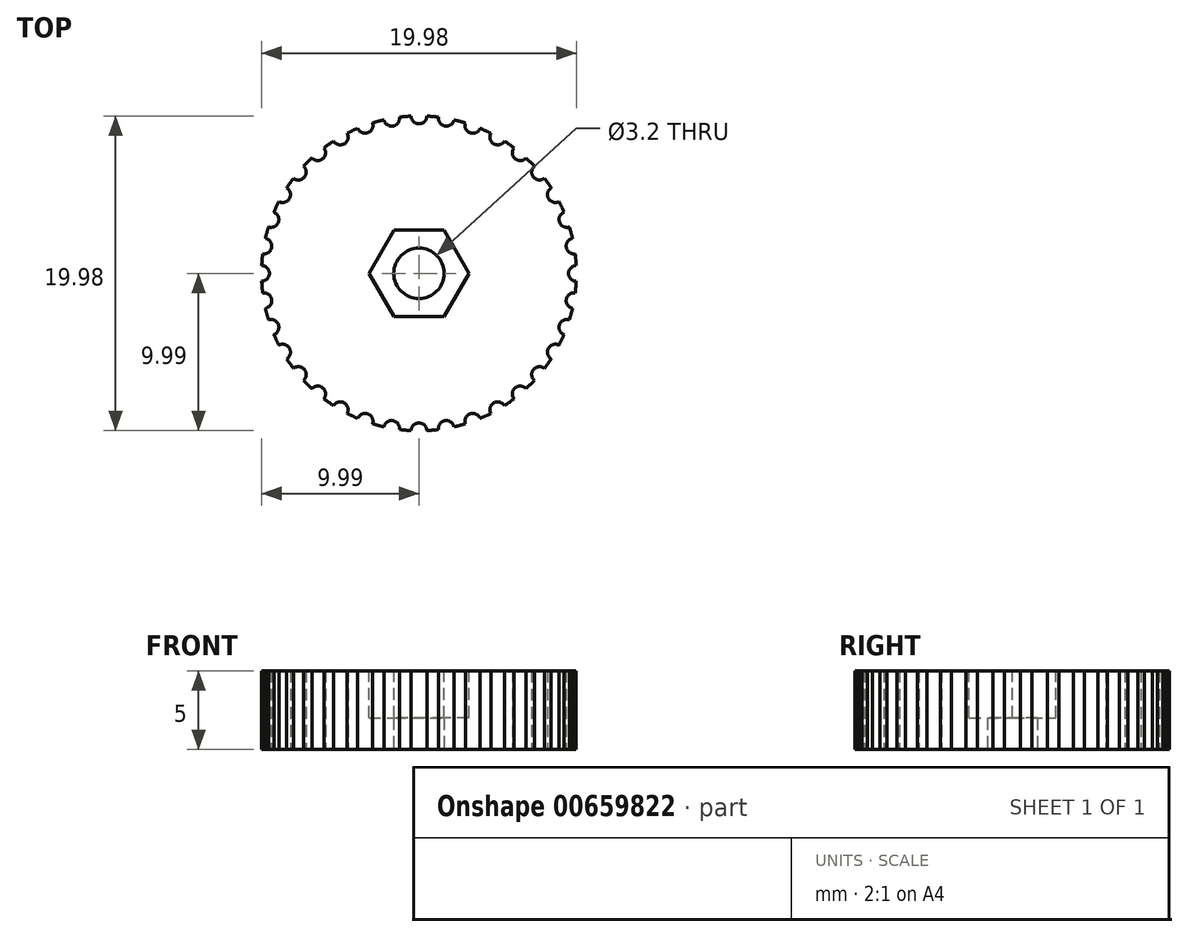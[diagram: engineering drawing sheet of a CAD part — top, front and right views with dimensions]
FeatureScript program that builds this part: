
annotation { "Feature Type Name" : "Feature", "Feature Type Description" : "" }
export const myFeature = defineFeature(function(context is Context, id is Id, definition is map)
    precondition{}
    {
        {
            var Q0;
            Q0=qCreatedBy(makeId("Top.planeOp"),FACE);
            var sketch = newSketch(context, id + "F0", { "sketchPlane" : qUnion([Q0])});
            skCircle(sketch, "E0", {"center": v(0, 0) * mm, "radius": 1.6 * mm});
            skArc(sketch, "E1", {"start": v(-0.5, 9.99) * mm, "mid": v(0, 9.5) * mm, "end": v(0.5, 9.99) * mm});
            skLineSegment(sketch, "E2.anchor1", {"start": v(0, 0) * mm, "end": v(0, 10) * mm, "construction": true});
            skArc(sketch, "E3", {"start": v(0.87, 9.96) * mm, "mid": v(0.69, 9.98) * mm, "end": v(0.5, 9.99) * mm});
            skLineSegment(sketch, "E4", {"start": v(0, 0) * mm, "end": v(0.87, 9.96) * mm, "construction": true});
            skLineSegment(sketch, "E5", {"start": v(0, 0) * mm, "end": v(-0.87, 9.96) * mm, "construction": true});
            skArc(sketch, "E6.trimOffspring", {"start": v(-0.5, 9.99) * mm, "mid": v(-0.69, 9.98) * mm, "end": v(-0.87, 9.96) * mm});
            skArc(sketch, "E7.1.0", {"start": v(-2.23, 9.75) * mm, "mid": v(-2.4, 9.7) * mm, "end": v(-2.59, 9.66) * mm});
            skArc(sketch, "E7.1.1", {"start": v(-2.23, 9.75) * mm, "mid": v(-1.65, 9.36) * mm, "end": v(-1.24, 9.92) * mm});
            skArc(sketch, "E7.1.2", {"start": v(-0.87, 9.96) * mm, "mid": v(-1.06, 9.94) * mm, "end": v(-1.24, 9.92) * mm});
            skArc(sketch, "E7.2.0", {"start": v(-3.89, 9.21) * mm, "mid": v(-4.06, 9.14) * mm, "end": v(-4.23, 9.06) * mm});
            skArc(sketch, "E7.2.1", {"start": v(-3.89, 9.21) * mm, "mid": v(-3.25, 8.93) * mm, "end": v(-2.95, 9.56) * mm});
            skArc(sketch, "E7.2.2", {"start": v(-2.59, 9.66) * mm, "mid": v(-2.77, 9.6) * mm, "end": v(-2.95, 9.56) * mm});
            skArc(sketch, "E7.3.0", {"start": v(-5.43, 8.4) * mm, "mid": v(-5.58, 8.3) * mm, "end": v(-5.74, 8.2) * mm});
            skArc(sketch, "E7.3.1", {"start": v(-5.43, 8.4) * mm, "mid": v(-4.75, 8.23) * mm, "end": v(-4.56, 8.9) * mm});
            skArc(sketch, "E7.3.2", {"start": v(-4.23, 9.06) * mm, "mid": v(-4.4, 8.98) * mm, "end": v(-4.56, 8.9) * mm});
            skArc(sketch, "E7.4.0", {"start": v(-6.8, 7.33) * mm, "mid": v(-6.94, 7.2) * mm, "end": v(-7.07, 7.07) * mm});
            skArc(sketch, "E7.4.1", {"start": v(-6.8, 7.33) * mm, "mid": v(-6.1, 7.28) * mm, "end": v(-6.04, 7.97) * mm});
            skArc(sketch, "E7.4.2", {"start": v(-5.74, 8.2) * mm, "mid": v(-5.89, 8.08) * mm, "end": v(-6.04, 7.97) * mm});
            skArc(sketch, "E7.5.0", {"start": v(-7.97, 6.04) * mm, "mid": v(-8.08, 5.89) * mm, "end": v(-8.2, 5.74) * mm});
            skArc(sketch, "E7.5.1", {"start": v(-7.97, 6.04) * mm, "mid": v(-7.28, 6.1) * mm, "end": v(-7.33, 6.8) * mm});
            skArc(sketch, "E7.5.2", {"start": v(-7.07, 7.07) * mm, "mid": v(-7.2, 6.94) * mm, "end": v(-7.33, 6.8) * mm});
            skArc(sketch, "E7.6.0", {"start": v(-8.9, 4.56) * mm, "mid": v(-8.98, 4.4) * mm, "end": v(-9.06, 4.23) * mm});
            skArc(sketch, "E7.6.1", {"start": v(-8.9, 4.56) * mm, "mid": v(-8.23, 4.75) * mm, "end": v(-8.4, 5.43) * mm});
            skArc(sketch, "E7.6.2", {"start": v(-8.2, 5.74) * mm, "mid": v(-8.3, 5.58) * mm, "end": v(-8.4, 5.43) * mm});
            skArc(sketch, "E7.7.0", {"start": v(-9.56, 2.95) * mm, "mid": v(-9.6, 2.77) * mm, "end": v(-9.66, 2.59) * mm});
            skArc(sketch, "E7.7.1", {"start": v(-9.56, 2.95) * mm, "mid": v(-8.93, 3.25) * mm, "end": v(-9.21, 3.89) * mm});
            skArc(sketch, "E7.7.2", {"start": v(-9.06, 4.23) * mm, "mid": v(-9.14, 4.06) * mm, "end": v(-9.21, 3.89) * mm});
            skArc(sketch, "E7.8.0", {"start": v(-9.92, 1.24) * mm, "mid": v(-9.94, 1.06) * mm, "end": v(-9.96, 0.87) * mm});
            skArc(sketch, "E7.8.1", {"start": v(-9.92, 1.24) * mm, "mid": v(-9.36, 1.65) * mm, "end": v(-9.75, 2.23) * mm});
            skArc(sketch, "E7.8.2", {"start": v(-9.66, 2.59) * mm, "mid": v(-9.7, 2.4) * mm, "end": v(-9.75, 2.23) * mm});
            skArc(sketch, "E7.9.0", {"start": v(-9.99, -0.5) * mm, "mid": v(-9.98, -0.69) * mm, "end": v(-9.96, -0.87) * mm});
            skArc(sketch, "E7.9.1", {"start": v(-9.99, -0.5) * mm, "mid": v(-9.5, 0) * mm, "end": v(-9.99, 0.5) * mm});
            skArc(sketch, "E7.9.2", {"start": v(-9.96, 0.87) * mm, "mid": v(-9.98, 0.69) * mm, "end": v(-9.99, 0.5) * mm});
            skArc(sketch, "E7.10.0", {"start": v(-9.75, -2.23) * mm, "mid": v(-9.7, -2.4) * mm, "end": v(-9.66, -2.59) * mm});
            skArc(sketch, "E7.10.1", {"start": v(-9.75, -2.23) * mm, "mid": v(-9.36, -1.65) * mm, "end": v(-9.92, -1.24) * mm});
            skArc(sketch, "E7.10.2", {"start": v(-9.96, -0.87) * mm, "mid": v(-9.94, -1.06) * mm, "end": v(-9.92, -1.24) * mm});
            skArc(sketch, "E7.11.0", {"start": v(-9.21, -3.89) * mm, "mid": v(-9.14, -4.06) * mm, "end": v(-9.06, -4.23) * mm});
            skArc(sketch, "E7.11.1", {"start": v(-9.21, -3.89) * mm, "mid": v(-8.93, -3.25) * mm, "end": v(-9.56, -2.95) * mm});
            skArc(sketch, "E7.11.2", {"start": v(-9.66, -2.59) * mm, "mid": v(-9.6, -2.77) * mm, "end": v(-9.56, -2.95) * mm});
            skArc(sketch, "E7.12.0", {"start": v(-8.4, -5.43) * mm, "mid": v(-8.3, -5.58) * mm, "end": v(-8.2, -5.74) * mm});
            skArc(sketch, "E7.12.1", {"start": v(-8.4, -5.43) * mm, "mid": v(-8.23, -4.75) * mm, "end": v(-8.9, -4.56) * mm});
            skArc(sketch, "E7.12.2", {"start": v(-9.06, -4.23) * mm, "mid": v(-8.98, -4.4) * mm, "end": v(-8.9, -4.56) * mm});
            skArc(sketch, "E7.13.0", {"start": v(-7.33, -6.8) * mm, "mid": v(-7.2, -6.94) * mm, "end": v(-7.07, -7.07) * mm});
            skArc(sketch, "E7.13.1", {"start": v(-7.33, -6.8) * mm, "mid": v(-7.28, -6.1) * mm, "end": v(-7.97, -6.04) * mm});
            skArc(sketch, "E7.13.2", {"start": v(-8.2, -5.74) * mm, "mid": v(-8.08, -5.89) * mm, "end": v(-7.97, -6.04) * mm});
            skArc(sketch, "E7.14.0", {"start": v(-6.04, -7.97) * mm, "mid": v(-5.89, -8.08) * mm, "end": v(-5.74, -8.2) * mm});
            skArc(sketch, "E7.14.1", {"start": v(-6.04, -7.97) * mm, "mid": v(-6.1, -7.28) * mm, "end": v(-6.8, -7.33) * mm});
            skArc(sketch, "E7.14.2", {"start": v(-7.07, -7.07) * mm, "mid": v(-6.94, -7.2) * mm, "end": v(-6.8, -7.33) * mm});
            skArc(sketch, "E7.15.0", {"start": v(-4.56, -8.9) * mm, "mid": v(-4.4, -8.98) * mm, "end": v(-4.23, -9.06) * mm});
            skArc(sketch, "E7.15.1", {"start": v(-4.56, -8.9) * mm, "mid": v(-4.75, -8.23) * mm, "end": v(-5.43, -8.4) * mm});
            skArc(sketch, "E7.15.2", {"start": v(-5.74, -8.2) * mm, "mid": v(-5.58, -8.3) * mm, "end": v(-5.43, -8.4) * mm});
            skArc(sketch, "E7.16.0", {"start": v(-2.95, -9.56) * mm, "mid": v(-2.77, -9.6) * mm, "end": v(-2.59, -9.66) * mm});
            skArc(sketch, "E7.16.1", {"start": v(-2.95, -9.56) * mm, "mid": v(-3.25, -8.93) * mm, "end": v(-3.89, -9.21) * mm});
            skArc(sketch, "E7.16.2", {"start": v(-4.23, -9.06) * mm, "mid": v(-4.06, -9.14) * mm, "end": v(-3.89, -9.21) * mm});
            skArc(sketch, "E7.17.0", {"start": v(-1.24, -9.92) * mm, "mid": v(-1.06, -9.94) * mm, "end": v(-0.87, -9.96) * mm});
            skArc(sketch, "E7.17.1", {"start": v(-1.24, -9.92) * mm, "mid": v(-1.65, -9.36) * mm, "end": v(-2.23, -9.75) * mm});
            skArc(sketch, "E7.17.2", {"start": v(-2.59, -9.66) * mm, "mid": v(-2.4, -9.7) * mm, "end": v(-2.23, -9.75) * mm});
            skArc(sketch, "E7.18.0", {"start": v(0.5, -9.99) * mm, "mid": v(0.69, -9.98) * mm, "end": v(0.87, -9.96) * mm});
            skArc(sketch, "E7.18.1", {"start": v(0.5, -9.99) * mm, "mid": v(0, -9.5) * mm, "end": v(-0.5, -9.99) * mm});
            skArc(sketch, "E7.18.2", {"start": v(-0.87, -9.96) * mm, "mid": v(-0.69, -9.98) * mm, "end": v(-0.5, -9.99) * mm});
            skArc(sketch, "E7.19.0", {"start": v(2.23, -9.75) * mm, "mid": v(2.4, -9.7) * mm, "end": v(2.59, -9.66) * mm});
            skArc(sketch, "E7.19.1", {"start": v(2.23, -9.75) * mm, "mid": v(1.65, -9.36) * mm, "end": v(1.24, -9.92) * mm});
            skArc(sketch, "E7.19.2", {"start": v(0.87, -9.96) * mm, "mid": v(1.06, -9.94) * mm, "end": v(1.24, -9.92) * mm});
            skArc(sketch, "E7.20.0", {"start": v(3.89, -9.21) * mm, "mid": v(4.06, -9.14) * mm, "end": v(4.23, -9.06) * mm});
            skArc(sketch, "E7.20.1", {"start": v(3.89, -9.21) * mm, "mid": v(3.25, -8.93) * mm, "end": v(2.95, -9.56) * mm});
            skArc(sketch, "E7.20.2", {"start": v(2.59, -9.66) * mm, "mid": v(2.77, -9.6) * mm, "end": v(2.95, -9.56) * mm});
            skArc(sketch, "E7.21.0", {"start": v(5.43, -8.4) * mm, "mid": v(5.58, -8.3) * mm, "end": v(5.74, -8.2) * mm});
            skArc(sketch, "E7.21.1", {"start": v(5.43, -8.4) * mm, "mid": v(4.75, -8.23) * mm, "end": v(4.56, -8.9) * mm});
            skArc(sketch, "E7.21.2", {"start": v(4.23, -9.06) * mm, "mid": v(4.4, -8.98) * mm, "end": v(4.56, -8.9) * mm});
            skArc(sketch, "E7.22.0", {"start": v(6.8, -7.33) * mm, "mid": v(6.94, -7.2) * mm, "end": v(7.07, -7.07) * mm});
            skArc(sketch, "E7.22.1", {"start": v(6.8, -7.33) * mm, "mid": v(6.1, -7.28) * mm, "end": v(6.04, -7.97) * mm});
            skArc(sketch, "E7.22.2", {"start": v(5.74, -8.2) * mm, "mid": v(5.89, -8.08) * mm, "end": v(6.04, -7.97) * mm});
            skArc(sketch, "E7.23.0", {"start": v(7.97, -6.04) * mm, "mid": v(8.08, -5.89) * mm, "end": v(8.2, -5.74) * mm});
            skArc(sketch, "E7.23.1", {"start": v(7.97, -6.04) * mm, "mid": v(7.28, -6.1) * mm, "end": v(7.33, -6.8) * mm});
            skArc(sketch, "E7.23.2", {"start": v(7.07, -7.07) * mm, "mid": v(7.2, -6.94) * mm, "end": v(7.33, -6.8) * mm});
            skArc(sketch, "E7.24.0", {"start": v(8.9, -4.56) * mm, "mid": v(8.98, -4.4) * mm, "end": v(9.06, -4.23) * mm});
            skArc(sketch, "E7.24.1", {"start": v(8.9, -4.56) * mm, "mid": v(8.23, -4.75) * mm, "end": v(8.4, -5.43) * mm});
            skArc(sketch, "E7.24.2", {"start": v(8.2, -5.74) * mm, "mid": v(8.3, -5.58) * mm, "end": v(8.4, -5.43) * mm});
            skArc(sketch, "E7.25.0", {"start": v(9.56, -2.95) * mm, "mid": v(9.6, -2.77) * mm, "end": v(9.66, -2.59) * mm});
            skArc(sketch, "E7.25.1", {"start": v(9.56, -2.95) * mm, "mid": v(8.93, -3.25) * mm, "end": v(9.21, -3.89) * mm});
            skArc(sketch, "E7.25.2", {"start": v(9.06, -4.23) * mm, "mid": v(9.14, -4.06) * mm, "end": v(9.21, -3.89) * mm});
            skArc(sketch, "E7.26.0", {"start": v(9.92, -1.24) * mm, "mid": v(9.94, -1.06) * mm, "end": v(9.96, -0.87) * mm});
            skArc(sketch, "E7.26.1", {"start": v(9.92, -1.24) * mm, "mid": v(9.36, -1.65) * mm, "end": v(9.75, -2.23) * mm});
            skArc(sketch, "E7.26.2", {"start": v(9.66, -2.59) * mm, "mid": v(9.7, -2.4) * mm, "end": v(9.75, -2.23) * mm});
            skArc(sketch, "E7.27.0", {"start": v(9.99, 0.5) * mm, "mid": v(9.98, 0.69) * mm, "end": v(9.96, 0.87) * mm});
            skArc(sketch, "E7.27.1", {"start": v(9.99, 0.5) * mm, "mid": v(9.5, 0) * mm, "end": v(9.99, -0.5) * mm});
            skArc(sketch, "E7.27.2", {"start": v(9.96, -0.87) * mm, "mid": v(9.98, -0.69) * mm, "end": v(9.99, -0.5) * mm});
            skArc(sketch, "E7.28.0", {"start": v(9.75, 2.23) * mm, "mid": v(9.7, 2.4) * mm, "end": v(9.66, 2.59) * mm});
            skArc(sketch, "E7.28.1", {"start": v(9.75, 2.23) * mm, "mid": v(9.36, 1.65) * mm, "end": v(9.92, 1.24) * mm});
            skArc(sketch, "E7.28.2", {"start": v(9.96, 0.87) * mm, "mid": v(9.94, 1.06) * mm, "end": v(9.92, 1.24) * mm});
            skArc(sketch, "E7.29.0", {"start": v(9.21, 3.89) * mm, "mid": v(9.14, 4.06) * mm, "end": v(9.06, 4.23) * mm});
            skArc(sketch, "E7.29.1", {"start": v(9.21, 3.89) * mm, "mid": v(8.93, 3.25) * mm, "end": v(9.56, 2.95) * mm});
            skArc(sketch, "E7.29.2", {"start": v(9.66, 2.59) * mm, "mid": v(9.6, 2.77) * mm, "end": v(9.56, 2.95) * mm});
            skArc(sketch, "E7.30.0", {"start": v(8.4, 5.43) * mm, "mid": v(8.3, 5.58) * mm, "end": v(8.2, 5.74) * mm});
            skArc(sketch, "E7.30.1", {"start": v(8.4, 5.43) * mm, "mid": v(8.23, 4.75) * mm, "end": v(8.9, 4.56) * mm});
            skArc(sketch, "E7.30.2", {"start": v(9.06, 4.23) * mm, "mid": v(8.98, 4.4) * mm, "end": v(8.9, 4.56) * mm});
            skArc(sketch, "E7.31.0", {"start": v(7.33, 6.8) * mm, "mid": v(7.2, 6.94) * mm, "end": v(7.07, 7.07) * mm});
            skArc(sketch, "E7.31.1", {"start": v(7.33, 6.8) * mm, "mid": v(7.28, 6.1) * mm, "end": v(7.97, 6.04) * mm});
            skArc(sketch, "E7.31.2", {"start": v(8.2, 5.74) * mm, "mid": v(8.08, 5.89) * mm, "end": v(7.97, 6.04) * mm});
            skArc(sketch, "E7.32.0", {"start": v(6.04, 7.97) * mm, "mid": v(5.89, 8.08) * mm, "end": v(5.74, 8.2) * mm});
            skArc(sketch, "E7.32.1", {"start": v(6.04, 7.97) * mm, "mid": v(6.1, 7.28) * mm, "end": v(6.8, 7.33) * mm});
            skArc(sketch, "E7.32.2", {"start": v(7.07, 7.07) * mm, "mid": v(6.94, 7.2) * mm, "end": v(6.8, 7.33) * mm});
            skArc(sketch, "E7.33.0", {"start": v(4.56, 8.9) * mm, "mid": v(4.4, 8.98) * mm, "end": v(4.23, 9.06) * mm});
            skArc(sketch, "E7.33.1", {"start": v(4.56, 8.9) * mm, "mid": v(4.75, 8.23) * mm, "end": v(5.43, 8.4) * mm});
            skArc(sketch, "E7.33.2", {"start": v(5.74, 8.2) * mm, "mid": v(5.58, 8.3) * mm, "end": v(5.43, 8.4) * mm});
            skArc(sketch, "E7.34.0", {"start": v(2.95, 9.56) * mm, "mid": v(2.77, 9.6) * mm, "end": v(2.59, 9.66) * mm});
            skArc(sketch, "E7.34.1", {"start": v(2.95, 9.56) * mm, "mid": v(3.25, 8.93) * mm, "end": v(3.89, 9.21) * mm});
            skArc(sketch, "E7.34.2", {"start": v(4.23, 9.06) * mm, "mid": v(4.06, 9.14) * mm, "end": v(3.89, 9.21) * mm});
            skArc(sketch, "E8.3.35.0", {"start": v(1.24, 9.92) * mm, "mid": v(1.06, 9.94) * mm, "end": v(0.87, 9.96) * mm});
            skArc(sketch, "E8.4.35.0", {"start": v(1.24, 9.92) * mm, "mid": v(1.65, 9.36) * mm, "end": v(2.23, 9.75) * mm});
            skArc(sketch, "E8.8.35.0", {"start": v(2.59, 9.66) * mm, "mid": v(2.4, 9.7) * mm, "end": v(2.23, 9.75) * mm});
            skSolve(sketch);
        }
        {
            var Q0;
            Q0=makeQuery(id+"F0.imprint","IMPRINT",FACE,{"disambiguationData":[TD([[makeQuery(id+"F0.imprint","IMPRINT",EDGE,{"derivedFrom":sQuery(id+"F0.wireOp",EDGE,"E0")}),-1.0]])]});
            extrude(context, id + "F1", {"entities" : qUnion([Q0]), "depth" : 5 * mm, "offsetDistance" : 25 * mm});
        }
        {
            var Q0;
            Q0=makeQuery(id+"F1.opExtrude","CAP_FACE",FACE,{"disambiguationData":[OSD([sQuery(id+"F0.wireOp",EDGE,"E0"),sQuery(id+"F0.wireOp",EDGE,"E1"),sQuery(id+"F0.wireOp",EDGE,"E3"),sQuery(id+"F0.wireOp",EDGE,"E6.trimOffspring"),sQuery(id+"F0.wireOp",EDGE,"E7.1.0"),sQuery(id+"F0.wireOp",EDGE,"E7.1.1"),sQuery(id+"F0.wireOp",EDGE,"E7.1.2"),sQuery(id+"F0.wireOp",EDGE,"E7.2.0"),sQuery(id+"F0.wireOp",EDGE,"E7.2.1"),sQuery(id+"F0.wireOp",EDGE,"E7.2.2"),sQuery(id+"F0.wireOp",EDGE,"E7.3.0"),sQuery(id+"F0.wireOp",EDGE,"E7.3.1"),sQuery(id+"F0.wireOp",EDGE,"E7.3.2"),sQuery(id+"F0.wireOp",EDGE,"E7.4.0"),sQuery(id+"F0.wireOp",EDGE,"E7.4.1"),sQuery(id+"F0.wireOp",EDGE,"E7.4.2"),sQuery(id+"F0.wireOp",EDGE,"E7.5.0"),sQuery(id+"F0.wireOp",EDGE,"E7.5.1"),sQuery(id+"F0.wireOp",EDGE,"E7.5.2"),sQuery(id+"F0.wireOp",EDGE,"E7.6.0"),sQuery(id+"F0.wireOp",EDGE,"E7.6.1"),sQuery(id+"F0.wireOp",EDGE,"E7.6.2"),sQuery(id+"F0.wireOp",EDGE,"E7.7.0"),sQuery(id+"F0.wireOp",EDGE,"E7.7.1"),sQuery(id+"F0.wireOp",EDGE,"E7.7.2"),sQuery(id+"F0.wireOp",EDGE,"E7.8.0"),sQuery(id+"F0.wireOp",EDGE,"E7.8.1"),sQuery(id+"F0.wireOp",EDGE,"E7.8.2"),sQuery(id+"F0.wireOp",EDGE,"E7.9.0"),sQuery(id+"F0.wireOp",EDGE,"E7.9.1"),sQuery(id+"F0.wireOp",EDGE,"E7.9.2"),sQuery(id+"F0.wireOp",EDGE,"E7.10.0"),sQuery(id+"F0.wireOp",EDGE,"E7.10.1"),sQuery(id+"F0.wireOp",EDGE,"E7.10.2"),sQuery(id+"F0.wireOp",EDGE,"E7.11.0"),sQuery(id+"F0.wireOp",EDGE,"E7.11.1"),sQuery(id+"F0.wireOp",EDGE,"E7.11.2"),sQuery(id+"F0.wireOp",EDGE,"E7.12.0"),sQuery(id+"F0.wireOp",EDGE,"E7.12.1"),sQuery(id+"F0.wireOp",EDGE,"E7.12.2"),sQuery(id+"F0.wireOp",EDGE,"E7.13.0"),sQuery(id+"F0.wireOp",EDGE,"E7.13.1"),sQuery(id+"F0.wireOp",EDGE,"E7.13.2"),sQuery(id+"F0.wireOp",EDGE,"E7.14.0"),sQuery(id+"F0.wireOp",EDGE,"E7.14.1"),sQuery(id+"F0.wireOp",EDGE,"E7.14.2"),sQuery(id+"F0.wireOp",EDGE,"E7.15.0"),sQuery(id+"F0.wireOp",EDGE,"E7.15.1"),sQuery(id+"F0.wireOp",EDGE,"E7.15.2"),sQuery(id+"F0.wireOp",EDGE,"E7.16.0"),sQuery(id+"F0.wireOp",EDGE,"E7.16.1"),sQuery(id+"F0.wireOp",EDGE,"E7.16.2"),sQuery(id+"F0.wireOp",EDGE,"E7.17.0"),sQuery(id+"F0.wireOp",EDGE,"E7.17.1"),sQuery(id+"F0.wireOp",EDGE,"E7.17.2"),sQuery(id+"F0.wireOp",EDGE,"E7.18.0"),sQuery(id+"F0.wireOp",EDGE,"E7.18.1"),sQuery(id+"F0.wireOp",EDGE,"E7.18.2"),sQuery(id+"F0.wireOp",EDGE,"E7.19.0"),sQuery(id+"F0.wireOp",EDGE,"E7.19.1"),sQuery(id+"F0.wireOp",EDGE,"E7.19.2"),sQuery(id+"F0.wireOp",EDGE,"E7.20.0"),sQuery(id+"F0.wireOp",EDGE,"E7.20.1"),sQuery(id+"F0.wireOp",EDGE,"E7.20.2"),sQuery(id+"F0.wireOp",EDGE,"E7.21.0"),sQuery(id+"F0.wireOp",EDGE,"E7.21.1"),sQuery(id+"F0.wireOp",EDGE,"E7.21.2"),sQuery(id+"F0.wireOp",EDGE,"E7.22.0"),sQuery(id+"F0.wireOp",EDGE,"E7.22.1"),sQuery(id+"F0.wireOp",EDGE,"E7.22.2"),sQuery(id+"F0.wireOp",EDGE,"E7.23.0"),sQuery(id+"F0.wireOp",EDGE,"E7.23.1"),sQuery(id+"F0.wireOp",EDGE,"E7.23.2"),sQuery(id+"F0.wireOp",EDGE,"E7.24.0"),sQuery(id+"F0.wireOp",EDGE,"E7.24.1"),sQuery(id+"F0.wireOp",EDGE,"E7.24.2"),sQuery(id+"F0.wireOp",EDGE,"E7.25.0"),sQuery(id+"F0.wireOp",EDGE,"E7.25.1"),sQuery(id+"F0.wireOp",EDGE,"E7.25.2"),sQuery(id+"F0.wireOp",EDGE,"E7.26.0"),sQuery(id+"F0.wireOp",EDGE,"E7.26.1"),sQuery(id+"F0.wireOp",EDGE,"E7.26.2"),sQuery(id+"F0.wireOp",EDGE,"E7.27.0"),sQuery(id+"F0.wireOp",EDGE,"E7.27.1"),sQuery(id+"F0.wireOp",EDGE,"E7.27.2"),sQuery(id+"F0.wireOp",EDGE,"E7.28.0"),sQuery(id+"F0.wireOp",EDGE,"E7.28.1"),sQuery(id+"F0.wireOp",EDGE,"E7.28.2"),sQuery(id+"F0.wireOp",EDGE,"E7.29.0"),sQuery(id+"F0.wireOp",EDGE,"E7.29.1"),sQuery(id+"F0.wireOp",EDGE,"E7.29.2"),sQuery(id+"F0.wireOp",EDGE,"E7.30.0"),sQuery(id+"F0.wireOp",EDGE,"E7.30.1"),sQuery(id+"F0.wireOp",EDGE,"E7.30.2"),sQuery(id+"F0.wireOp",EDGE,"E7.31.0"),sQuery(id+"F0.wireOp",EDGE,"E7.31.1"),sQuery(id+"F0.wireOp",EDGE,"E7.31.2"),sQuery(id+"F0.wireOp",EDGE,"E7.32.0"),sQuery(id+"F0.wireOp",EDGE,"E7.32.1"),sQuery(id+"F0.wireOp",EDGE,"E7.32.2"),sQuery(id+"F0.wireOp",EDGE,"E7.33.0"),sQuery(id+"F0.wireOp",EDGE,"E7.33.1"),sQuery(id+"F0.wireOp",EDGE,"E7.33.2"),sQuery(id+"F0.wireOp",EDGE,"E7.34.0"),sQuery(id+"F0.wireOp",EDGE,"E7.34.1"),sQuery(id+"F0.wireOp",EDGE,"E7.34.2"),sQuery(id+"F0.wireOp",EDGE,"E8.3.35.0"),sQuery(id+"F0.wireOp",EDGE,"E8.4.35.0"),sQuery(id+"F0.wireOp",EDGE,"E8.8.35.0")])],"isStart":false});
            var sketch = newSketch(context, id + "F2", { "sketchPlane" : qUnion([Q0])});
            skCircle(sketch, "E9.cCircle", {"center": v(0, 0) * mm, "radius": 2.75 * mm, "construction": true});
            skLineSegment(sketch, "E9.0", {"start": v(-1.59, 2.75) * mm, "end": v(1.59, 2.75) * mm});
            skLineSegment(sketch, "E9.1", {"start": v(1.59, 2.75) * mm, "end": v(3.18, 0) * mm});
            skLineSegment(sketch, "E9.2", {"start": v(3.18, 0) * mm, "end": v(1.59, -2.75) * mm});
            skLineSegment(sketch, "E9.3", {"start": v(1.59, -2.75) * mm, "end": v(-1.59, -2.75) * mm});
            skLineSegment(sketch, "E9.4", {"start": v(-1.59, -2.75) * mm, "end": v(-3.18, 0) * mm});
            skLineSegment(sketch, "E9.5", {"start": v(-3.18, 0) * mm, "end": v(-1.59, 2.75) * mm});
            skPoint(sketch, "E9.0.midPoint", {"position": v(0, 2.75) * mm});
            skSolve(sketch);
        }
        {
            var Q0;
            Q0=makeQuery(id+"F2.imprint","IMPRINT",FACE,{"disambiguationData":[TD([[makeQuery(id+"F2.imprint","IMPRINT",EDGE,{"derivedFrom":sQuery(id+"F2.wireOp",EDGE,"E9.0")}),-1.0]])]});
            extrude(context, id + "F3", {"entities" : qUnion([Q0]), "operationType" : NewBodyOperationType.REMOVE, "oppositeDirection" : true, "depth" : 3 * mm, "offsetDistance" : 25 * mm});
        }
    });
